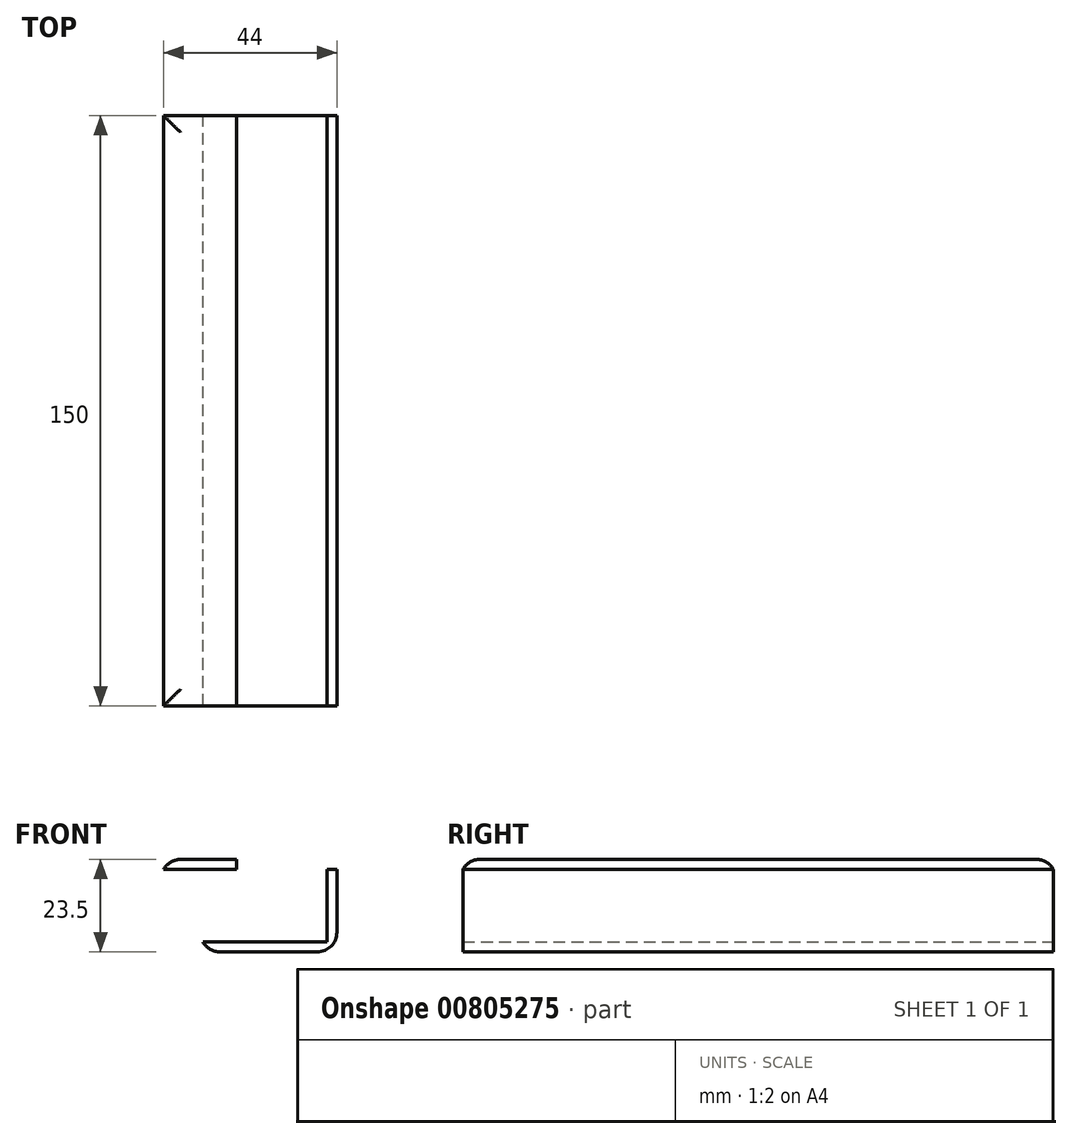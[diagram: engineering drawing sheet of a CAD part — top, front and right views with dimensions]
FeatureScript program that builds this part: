
annotation { "Feature Type Name" : "Feature", "Feature Type Description" : "" }
export const myFeature = defineFeature(function(context is Context, id is Id, definition is map)
    precondition{}
    {
        {
            var Q0;
            Q0=qCreatedBy(makeId("Front.planeOp"),FACE);
            var sketch = newSketch(context, id + "F0", { "sketchPlane" : qUnion([Q0])});
            skLineSegment(sketch, "E0", {"start": v(0, 0) * mm, "end": v(0, 27) * mm, "construction": true});
            skLineSegment(sketch, "E1", {"start": v(0, 0) * mm, "end": v(0, -21) * mm, "construction": true});
            skLineSegment(sketch, "E2.bottom", {"start": v(0, -21) * mm, "end": v(-17, -21) * mm});
            skLineSegment(sketch, "E2.top", {"start": v(0, -18.5) * mm, "end": v(-17, -18.5) * mm});
            skLineSegment(sketch, "E2.left", {"start": v(0, -21) * mm, "end": v(0, -18.5) * mm});
            skLineSegment(sketch, "E2.right", {"start": v(-17, -21) * mm, "end": v(-17, -18.5) * mm});
            skLineSegment(sketch, "E3.bottom", {"start": v(-17, -18.5) * mm, "end": v(-14.5, -18.5) * mm});
            skLineSegment(sketch, "E3.top", {"start": v(-17, 0) * mm, "end": v(-14.5, 0) * mm});
            skLineSegment(sketch, "E3.left", {"start": v(-17, -18.5) * mm, "end": v(-17, 0) * mm});
            skLineSegment(sketch, "E3.right", {"start": v(-14.5, -18.5) * mm, "end": v(-14.5, 0) * mm});
            skLineSegment(sketch, "E4.bottom", {"start": v(-14.5, 0) * mm, "end": v(-27, 0) * mm});
            skLineSegment(sketch, "E4.top", {"start": v(-14.5, 2.5) * mm, "end": v(-27, 2.5) * mm});
            skLineSegment(sketch, "E4.left", {"start": v(-14.5, 0) * mm, "end": v(-14.5, 2.5) * mm});
            skLineSegment(sketch, "E4.right", {"start": v(-27, 0) * mm, "end": v(-27, 2.5) * mm});
            skLineSegment(sketch, "E5.bottom", {"start": v(-14.5, 2.5) * mm, "end": v(-8.5, 2.5) * mm});
            skLineSegment(sketch, "E5.top", {"start": v(-14.5, 0) * mm, "end": v(-8.5, 0) * mm});
            skLineSegment(sketch, "E5.left", {"start": v(-14.5, 2.5) * mm, "end": v(-14.5, 0) * mm});
            skLineSegment(sketch, "E5.right", {"start": v(-8.5, 2.5) * mm, "end": v(-8.5, 0) * mm});
            skLineSegment(sketch, "E6.bottom", {"start": v(-8.5, 0) * mm, "end": v(-11, 0) * mm});
            skLineSegment(sketch, "E6.top", {"start": v(-8.5, -18.5) * mm, "end": v(-11, -18.5) * mm});
            skLineSegment(sketch, "E6.left", {"start": v(-8.5, 0) * mm, "end": v(-8.5, -18.5) * mm});
            skLineSegment(sketch, "E6.right", {"start": v(-11, 0) * mm, "end": v(-11, -18.5) * mm});
            skLineSegment(sketch, "E7.MirrorCS", {"start": v(14.5, 0) * mm, "end": v(14.5, 2.5) * mm});
            skLineSegment(sketch, "E8.MirrorCS", {"start": v(14.5, 2.5) * mm, "end": v(14.5, 0) * mm});
            skLineSegment(sketch, "E9.MirrorCS", {"start": v(17, 0) * mm, "end": v(14.5, 0) * mm});
            skLineSegment(sketch, "E10.MirrorCS", {"start": v(8.5, -18.5) * mm, "end": v(11, -18.5) * mm});
            skLineSegment(sketch, "E11.MirrorCS", {"start": v(8.5, 2.5) * mm, "end": v(8.5, 0) * mm});
            skLineSegment(sketch, "E12.MirrorCS", {"start": v(27, 0) * mm, "end": v(27, 2.5) * mm});
            skLineSegment(sketch, "E13.MirrorCS", {"start": v(14.5, 0) * mm, "end": v(8.5, 0) * mm});
            skLineSegment(sketch, "E14.MirrorCS", {"start": v(17, -18.5) * mm, "end": v(14.5, -18.5) * mm});
            skLineSegment(sketch, "E15.MirrorCS", {"start": v(8.5, 0) * mm, "end": v(11, 0) * mm});
            skLineSegment(sketch, "E16.MirrorCS", {"start": v(17, -21) * mm, "end": v(17, -18.5) * mm});
            skLineSegment(sketch, "E17.MirrorCS", {"start": v(17, -18.5) * mm, "end": v(17, 0) * mm});
            skLineSegment(sketch, "E18.MirrorCS", {"start": v(11, 0) * mm, "end": v(11, -18.5) * mm});
            skLineSegment(sketch, "E19.MirrorCS", {"start": v(0, -18.5) * mm, "end": v(17, -18.5) * mm});
            skLineSegment(sketch, "E20.MirrorCS", {"start": v(14.5, 2.5) * mm, "end": v(8.5, 2.5) * mm});
            skLineSegment(sketch, "E21.MirrorCS", {"start": v(0, -21) * mm, "end": v(17, -21) * mm});
            skLineSegment(sketch, "E22.MirrorCS", {"start": v(8.5, 0) * mm, "end": v(8.5, -18.5) * mm});
            skLineSegment(sketch, "E23.MirrorCS", {"start": v(14.5, -18.5) * mm, "end": v(14.5, 0) * mm});
            skLineSegment(sketch, "E24.MirrorCS", {"start": v(14.5, 2.5) * mm, "end": v(27, 2.5) * mm});
            skLineSegment(sketch, "E25.MirrorCS", {"start": v(14.5, 0) * mm, "end": v(27, 0) * mm});
            skSolve(sketch);
        }
        {
            var Q0;
            Q0=makeQuery(id+"F0.imprint","IMPRINT",FACE,{"disambiguationData":[TD([[makeQuery(id+"F0.imprint","IMPRINT",EDGE,{"derivedFrom":sQuery(id+"F0.wireOp",EDGE,"E4.top")}),1.0]])]});
            var Q1;
            Q1=makeQuery(id+"F0.imprint","IMPRINT",FACE,{"disambiguationData":[TD([[makeQuery(id+"F0.imprint","IMPRINT",EDGE,{"derivedFrom":sQuery(id+"F0.wireOp",EDGE,"E5.bottom")}),-1.0]])]});
            var Q2;
            Q2=makeQuery(id+"F0.imprint","IMPRINT",FACE,{"disambiguationData":[TD([[makeQuery(id+"F0.imprint","IMPRINT",EDGE,{"derivedFrom":sQuery(id+"F0.wireOp",EDGE,"E6.bottom")}),1.0]])]});
            var Q3;
            Q3=makeQuery(id+"F0.imprint","IMPRINT",FACE,{"disambiguationData":[TD([[makeQuery(id+"F0.imprint","IMPRINT",EDGE,{"derivedFrom":sQuery(id+"F0.wireOp",EDGE,"E3.bottom")}),1.0]])]});
            var Q4;
            Q4=makeQuery(id+"F0.imprint","IMPRINT",FACE,{"disambiguationData":[TD([[makeQuery(id+"F0.imprint","IMPRINT",EDGE,{"derivedFrom":sQuery(id+"F0.wireOp",EDGE,"E2.bottom")}),-1.0]])]});
            var Q5;
            {var subQ4=sQuery(id+"F0.wireOp",EDGE,"E16.MirrorCS");Q5=makeQuery(id+"F0.imprint","IMPRINT",FACE,{"disambiguationData":[TD([[makeQuery(id+"F0.imprint","IMPRINT",EDGE,{"derivedFrom":subQ4}),1.0]])]});}
            var Q6;
            Q6=makeQuery(id+"F0.imprint","IMPRINT",FACE,{"disambiguationData":[TD([[makeQuery(id+"F0.imprint","IMPRINT",EDGE,{"derivedFrom":sQuery(id+"F0.wireOp",EDGE,"E15.MirrorCS")}),-1.0]])]});
            var Q7;
            {var subQ0=sQuery(id+"F0.wireOp",EDGE,"E17.MirrorCS");Q7=makeQuery(id+"F0.imprint","IMPRINT",FACE,{"disambiguationData":[TD([[makeQuery(id+"F0.imprint","IMPRINT",EDGE,{"derivedFrom":subQ0}),1.0]])]});}
            var Q8;
            {var subQ1=sQuery(id+"F0.wireOp",EDGE,"E8.MirrorCS");Q8=makeQuery(id+"F0.imprint","IMPRINT",FACE,{"disambiguationData":[TD([[makeQuery(id+"F0.imprint","IMPRINT",EDGE,{"derivedFrom":subQ1}),1.0]])]});}
            var Q9;
            Q9=makeQuery(id+"F0.imprint","IMPRINT",FACE,{"disambiguationData":[TD([[makeQuery(id+"F0.imprint","IMPRINT",EDGE,{"derivedFrom":sQuery(id+"F0.wireOp",EDGE,"E8.MirrorCS")}),-1.0]])]});
            extrude(context, id + "F1", {"entities" : qUnion([Q0, Q1, Q2, Q3, Q4, Q5, Q6, Q7, Q8, Q9]), "depth" : 150 * mm, "offsetDistance" : 25 * mm});
        }
        {
            var Q0;
            Q0=makeQuery(id+"F1.opExtrude","SWEPT_EDGE",EDGE,{"disambiguationData":[OSD([sQuery(id+"F0.wireOp",EDGE,"E2.bottom"),sQuery(id+"F0.wireOp",EDGE,"E2.right")])]});
            var Q1;
            Q1=makeQuery(id+"F1.opExtrude","SWEPT_EDGE",EDGE,{"disambiguationData":[OSD([sQuery(id+"F0.wireOp",EDGE,"E16.MirrorCS"),sQuery(id+"F0.wireOp",EDGE,"E21.MirrorCS")])]});
            var Q2;
            Q2=makeQuery(id+"F1.opExtrude","SWEPT_EDGE",EDGE,{"disambiguationData":[OSD([sQuery(id+"F0.wireOp",EDGE,"E4.top"),sQuery(id+"F0.wireOp",EDGE,"E4.right")])]});
            var Q3;
            Q3=makeQuery(id+"F1.opExtrude","CAP_EDGE",EDGE,{"disambiguationData":[OSD([sQuery(id+"F0.wireOp",EDGE,"E4.top"),sQuery(id+"F0.wireOp",EDGE,"E5.bottom")])],"isStart":false});
            var Q4;
            Q4=makeQuery(id+"F1.opExtrude","CAP_EDGE",EDGE,{"disambiguationData":[OSD([sQuery(id+"F0.wireOp",EDGE,"E20.MirrorCS"),sQuery(id+"F0.wireOp",EDGE,"E24.MirrorCS")])],"isStart":false});
            var Q5;
            Q5=makeQuery(id+"F1.opExtrude","SWEPT_EDGE",EDGE,{"disambiguationData":[OSD([sQuery(id+"F0.wireOp",EDGE,"E12.MirrorCS"),sQuery(id+"F0.wireOp",EDGE,"E24.MirrorCS")])]});
            var Q6;
            Q6=makeQuery(id+"F1.opExtrude","CAP_EDGE",EDGE,{"disambiguationData":[OSD([sQuery(id+"F0.wireOp",EDGE,"E20.MirrorCS"),sQuery(id+"F0.wireOp",EDGE,"E24.MirrorCS")])],"isStart":true});
            var Q7;
            Q7=makeQuery(id+"F1.opExtrude","CAP_EDGE",EDGE,{"disambiguationData":[OSD([sQuery(id+"F0.wireOp",EDGE,"E4.top"),sQuery(id+"F0.wireOp",EDGE,"E5.bottom")])],"isStart":true});
            fillet(context, id + "F2", {"entities" : qUnion([Q0, Q1, Q2, Q3, Q4, Q5, Q6, Q7]), "radius" : 5 * mm, "tangentPropagation" : true, "allowEdgeOverflow" : false});
        }
    });
